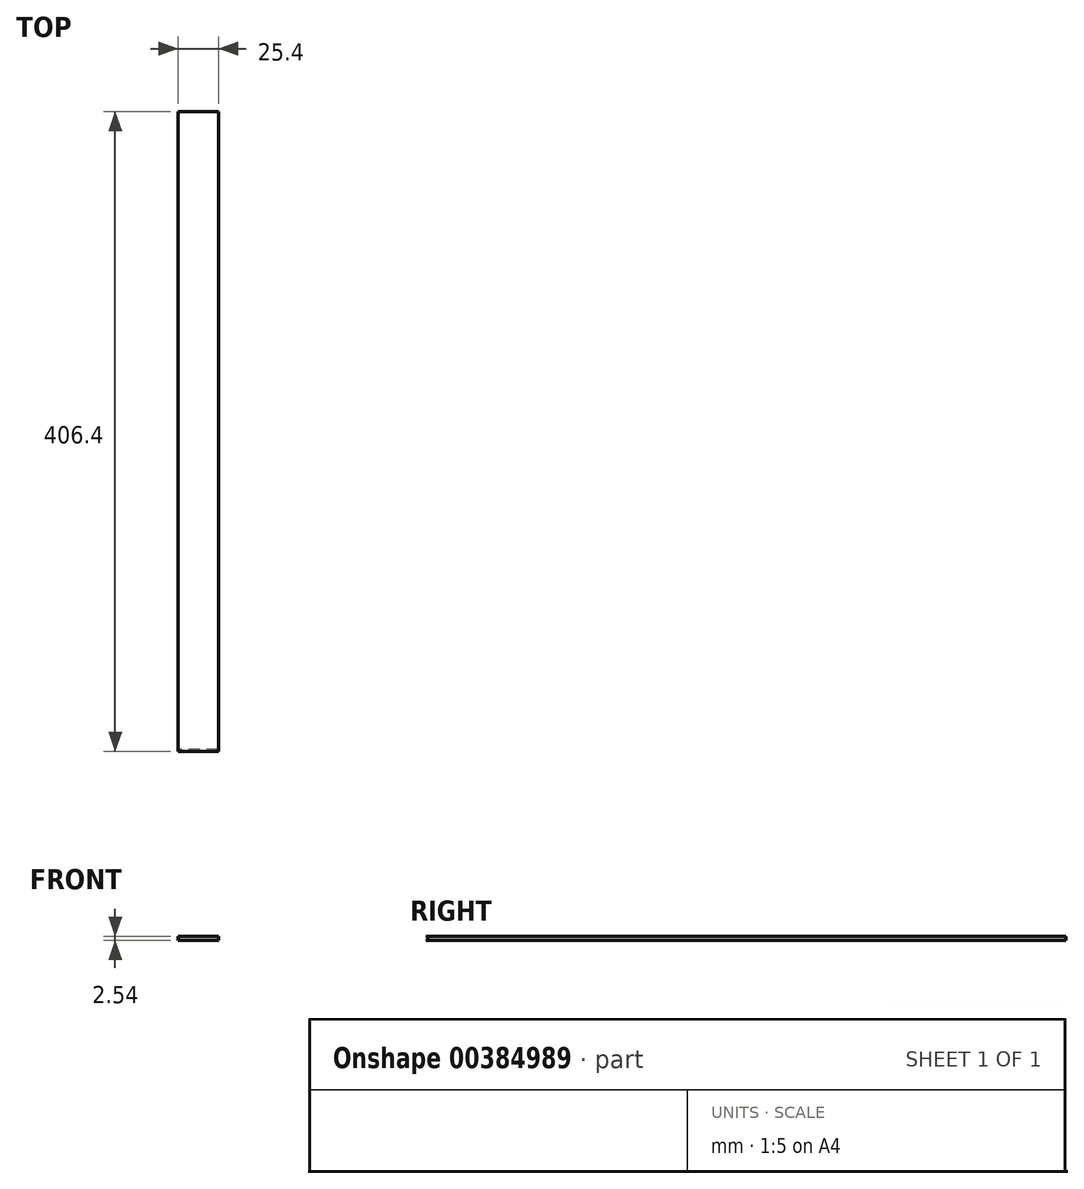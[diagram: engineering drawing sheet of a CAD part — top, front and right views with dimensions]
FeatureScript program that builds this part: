
annotation { "Feature Type Name" : "Feature", "Feature Type Description" : "" }
export const myFeature = defineFeature(function(context is Context, id is Id, definition is map)
    precondition{}
    {
        {
            var Q0;
            Q0=qCreatedBy(makeId("Right.planeOp"),FACE);
            var sketch = newSketch(context, id + "F0", { "sketchPlane" : qUnion([Q0])});
            skCircle(sketch, "E0", {"center": v(0, 0) * mm, "radius": 1.27 * mm});
            skLineSegment(sketch, "E1.bottom", {"start": v(0, 1.27) * mm, "end": v(406.4, 1.27) * mm});
            skLineSegment(sketch, "E1.top", {"start": v(0, -1.27) * mm, "end": v(406.4, -1.27) * mm});
            skLineSegment(sketch, "E1.left", {"start": v(0, 1.27) * mm, "end": v(0, -1.27) * mm});
            skLineSegment(sketch, "E1.right", {"start": v(406.4, 1.27) * mm, "end": v(406.4, -1.27) * mm});
            skSolve(sketch);
        }
        {
            var Q0;
            {var subQ1=sQuery(id+"F0.wireOp",EDGE,"E1.bottom");Q0=makeQuery(id+"F0.imprint","IMPRINT",FACE,{"disambiguationData":[TD([[makeQuery(id+"F0.imprint","IMPRINT",EDGE,{"derivedFrom":subQ1}),-1.0]])]});}
            extrude(context, id + "F1", {"entities" : qUnion([Q0]), "endBound" : BoundingType.SYMMETRIC, "depth" : 25.4 * mm, "offsetDistance" : 25.4 * mm});
        }
    });
